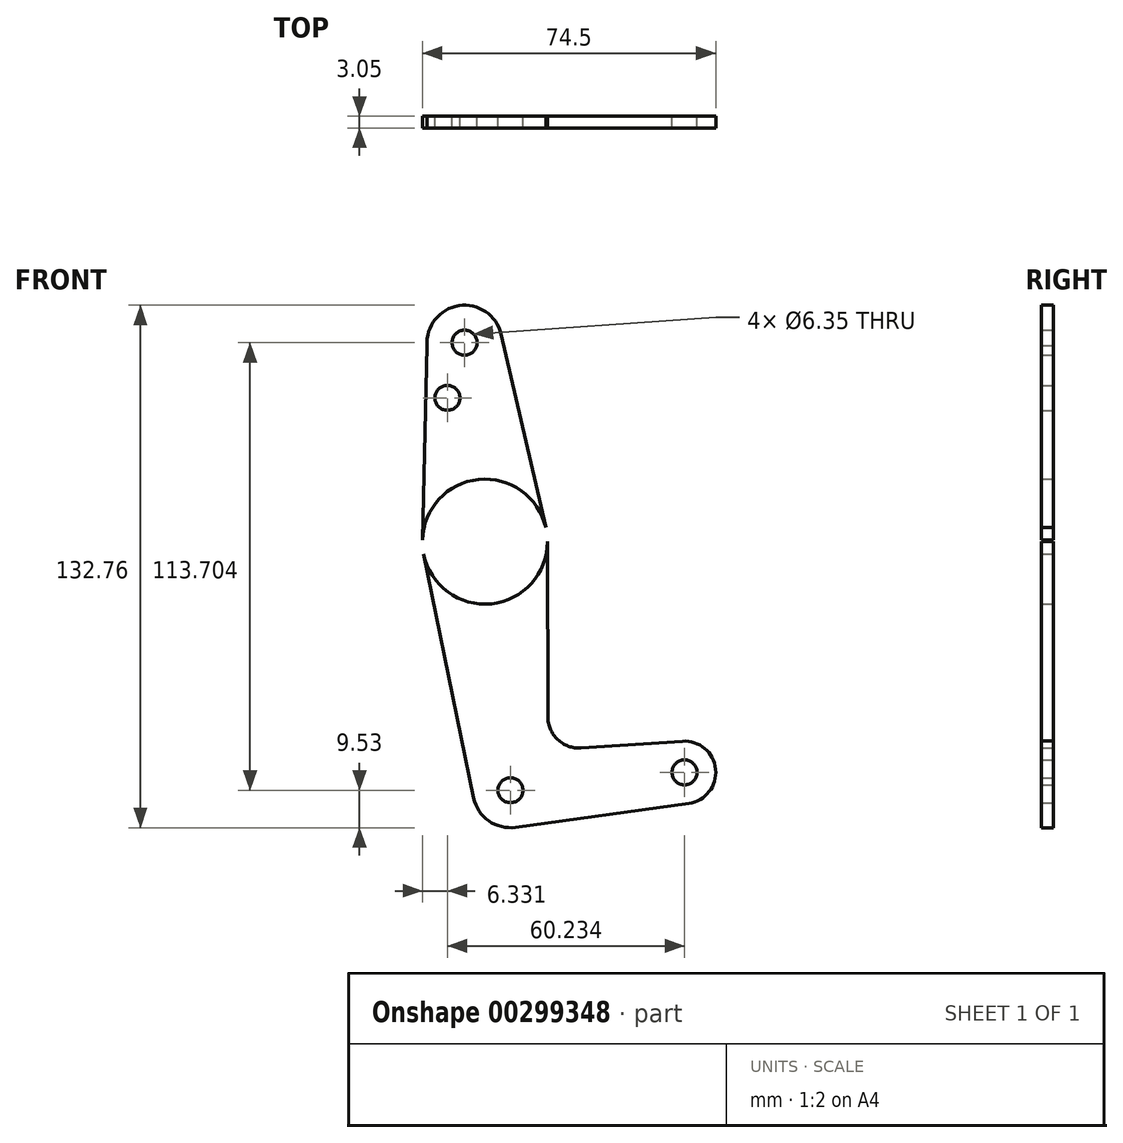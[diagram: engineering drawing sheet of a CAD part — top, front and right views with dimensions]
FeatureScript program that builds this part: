
annotation { "Feature Type Name" : "Feature", "Feature Type Description" : "" }
export const myFeature = defineFeature(function(context is Context, id is Id, definition is map)
    precondition{}
    {
        {
            var Q0;
            Q0=qCreatedBy(makeId("Front.planeOp"),FACE);
            var sketch = newSketch(context, id + "F0", { "sketchPlane" : qUnion([Q0])});
            skLineSegment(sketch, "E0", {"start": v(-72.08, 75.41) * mm, "end": v(-60.41, -38.3) * mm});
            skLineSegment(sketch, "E1", {"start": v(-60.41, -38.3) * mm, "end": v(-16.2, -33.76) * mm});
            skCircle(sketch, "E2", {"center": v(-66.9, 24.88) * mm, "radius": 15.88 * mm});
            skCircle(sketch, "E3", {"center": v(-72.08, 75.41) * mm, "radius": 9.53 * mm});
            skCircle(sketch, "E4", {"center": v(-60.41, -38.3) * mm, "radius": 9.53 * mm});
            skCircle(sketch, "E5", {"center": v(-16.2, -33.76) * mm, "radius": 7.94 * mm});
            skLineSegment(sketch, "E6", {"start": v(-81.57, 74.65) * mm, "end": v(-82.76, 25.26) * mm});
            skLineSegment(sketch, "E7", {"start": v(-82.44, 21.69) * mm, "end": v(-69.74, -40.2) * mm});
            skLineSegment(sketch, "E8", {"start": v(-59.1, -47.72) * mm, "end": v(-15.1, -41.62) * mm});
            skLineSegment(sketch, "E9", {"start": v(-16.72, -25.84) * mm, "end": v(-42.45, -27.55) * mm});
            skLineSegment(sketch, "E10", {"start": v(-50.93, -19.63) * mm, "end": v(-51.02, 24.91) * mm});
            skLineSegment(sketch, "E11", {"start": v(-51.43, 28.46) * mm, "end": v(-62.8, 77.56) * mm});
            skCircle(sketch, "E12", {"center": v(-72.08, 75.41) * mm, "radius": 3.18 * mm});
            skCircle(sketch, "E13", {"center": v(-66.9, 24.88) * mm, "radius": 3.18 * mm});
            skCircle(sketch, "E14", {"center": v(-60.41, -38.3) * mm, "radius": 3.18 * mm});
            skCircle(sketch, "E15", {"center": v(-16.2, -33.76) * mm, "radius": 3.18 * mm});
            skCircle(sketch, "E16", {"center": v(-76.43, 61.4) * mm, "radius": 3.18 * mm});
            skArc(sketch, "E17.filletArc", {"start": v(-50.93, -19.63) * mm, "mid": v(-48.4, -25.43) * mm, "end": v(-42.45, -27.55) * mm});
            skSolve(sketch);
        }
        {
            var Q0;
            {var subQ12=sQuery(id+"F0.wireOp",EDGE,"E9");Q0=makeQuery(id+"F0.imprint","IMPRINT",FACE,{"disambiguationData":[TD([[makeQuery(id+"F0.imprint","IMPRINT",EDGE,{"derivedFrom":subQ12}),1.0]])]});}
            var Q1;
            {var subQ5=sQuery(id+"F0.wireOp",EDGE,"E7");Q1=makeQuery(id+"F0.imprint","IMPRINT",FACE,{"disambiguationData":[TD([[makeQuery(id+"F0.imprint","IMPRINT",EDGE,{"derivedFrom":subQ5}),1.0]])]});}
            var Q2;
            {var subQ0=sQuery(id+"F0.wireOp",EDGE,"E4");var subQ3=sQuery(id+"F0.wireOp",EDGE,"E0");var subQ4=makeQuery(id+"F0.imprint","INTERSECT",VERTEX,{"derivedFrom":[subQ3,subQ0]});Q2=makeQuery(id+"F0.imprint","IMPRINT",FACE,{"disambiguationData":[TD([[makeQuery(id+"F0.imprint","IMPRINT",EDGE,{"disambiguationData":[TD([[subQ4,-1.0]])],"derivedFrom":subQ3}),-1.0]])]});}
            var Q3;
            {var subQ0=sQuery(id+"F0.wireOp",EDGE,"E4");var subQ1=sQuery(id+"F0.wireOp",EDGE,"E0");var subQ2=makeQuery(id+"F0.imprint","INTERSECT",VERTEX,{"derivedFrom":[subQ1,subQ0]});Q3=makeQuery(id+"F0.imprint","IMPRINT",FACE,{"disambiguationData":[TD([[makeQuery(id+"F0.imprint","IMPRINT",EDGE,{"disambiguationData":[TD([[subQ2,-1.0]])],"derivedFrom":subQ1}),1.0]])]});}
            var Q4;
            {var subQ5=sQuery(id+"F0.wireOp",EDGE,"E8");Q4=makeQuery(id+"F0.imprint","IMPRINT",FACE,{"disambiguationData":[TD([[makeQuery(id+"F0.imprint","IMPRINT",EDGE,{"derivedFrom":subQ5}),1.0]])]});}
            var Q5;
            Q5=makeQuery(id+"F0.imprint","IMPRINT",FACE,{"disambiguationData":[TD([[makeQuery(id+"F0.imprint","IMPRINT",EDGE,{"derivedFrom":sQuery(id+"F0.wireOp",EDGE,"E15")}),-1.0]])]});
            var Q6;
            {var subQ1=sQuery(id+"F0.wireOp",EDGE,"E2");var subQ5=sQuery(id+"F0.wireOp",EDGE,"E0");var subQ10=makeQuery(id+"F0.imprint","INTERSECT",VERTEX,{"disambiguationData":[OD(0.0)],"derivedFrom":[subQ5,subQ1]});Q6=makeQuery(id+"F0.imprint","IMPRINT",FACE,{"disambiguationData":[TD([[makeQuery(id+"F0.imprint","IMPRINT",EDGE,{"disambiguationData":[TD([[subQ10,-1.0]])],"derivedFrom":subQ5}),1.0]])]});}
            var Q7;
            {var subQ5=sQuery(id+"F0.wireOp",EDGE,"E11");Q7=makeQuery(id+"F0.imprint","IMPRINT",FACE,{"disambiguationData":[TD([[makeQuery(id+"F0.imprint","IMPRINT",EDGE,{"derivedFrom":subQ5}),1.0]])]});}
            var Q8;
            {var subQ0=sQuery(id+"F0.wireOp",EDGE,"E6");Q8=makeQuery(id+"F0.imprint","IMPRINT",FACE,{"disambiguationData":[TD([[makeQuery(id+"F0.imprint","IMPRINT",EDGE,{"derivedFrom":subQ0}),1.0]])]});}
            var Q9;
            Q9=makeQuery(id+"F0.imprint","IMPRINT",FACE,{"disambiguationData":[TD([[makeQuery(id+"F0.imprint","IMPRINT",EDGE,{"derivedFrom":sQuery(id+"F0.wireOp",EDGE,"E12")}),-1.0]])]});
            var Q10;
            {var subQ0=sQuery(id+"F0.wireOp",EDGE,"E2");var subQ4=sQuery(id+"F0.wireOp",EDGE,"E0");var subQ7=makeQuery(id+"F0.imprint","INTERSECT",VERTEX,{"disambiguationData":[OD(0.0)],"derivedFrom":[subQ4,subQ0]});Q10=makeQuery(id+"F0.imprint","IMPRINT",FACE,{"disambiguationData":[TD([[makeQuery(id+"F0.imprint","IMPRINT",EDGE,{"disambiguationData":[TD([[subQ7,-1.0]])],"derivedFrom":subQ4}),-1.0]])]});}
            extrude(context, id + "F1", {"entities" : qUnion([Q0, Q1, Q2, Q3, Q4, Q5, Q6, Q7, Q8, Q9, Q10]), "depth" : 3.05 * mm});
        }
    });
